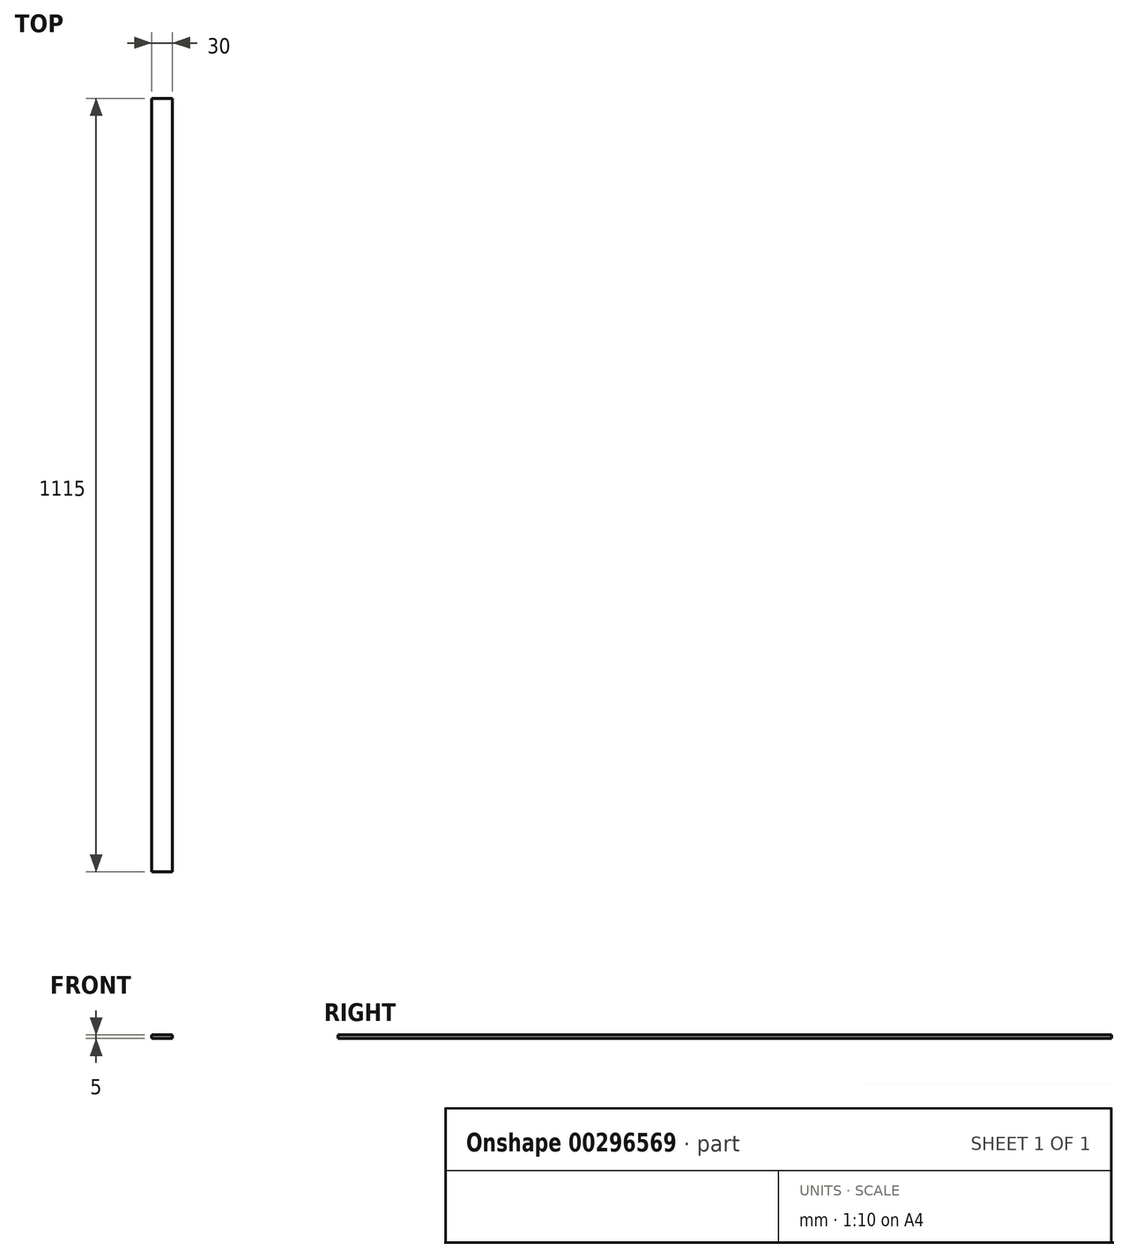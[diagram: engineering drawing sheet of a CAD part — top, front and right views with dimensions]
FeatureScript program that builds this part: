
annotation { "Feature Type Name" : "Feature", "Feature Type Description" : "" }
export const myFeature = defineFeature(function(context is Context, id is Id, definition is map)
    precondition{}
    {
        {
            var Q0;
            Q0=qCreatedBy(makeId("Top.planeOp"),FACE);
            var sketch = newSketch(context, id + "F0", { "sketchPlane" : qUnion([Q0])});
            skLineSegment(sketch, "E0.bottom", {"start": v(15, -557.5) * mm, "end": v(-15, -557.5) * mm});
            skLineSegment(sketch, "E0.top", {"start": v(15, 557.5) * mm, "end": v(-15, 557.5) * mm});
            skLineSegment(sketch, "E0.left", {"start": v(15, -557.5) * mm, "end": v(15, 557.5) * mm});
            skLineSegment(sketch, "E0.right", {"start": v(-15, -557.5) * mm, "end": v(-15, 557.5) * mm});
            skPoint(sketch, "E0.middle", {"position": v(0, 0) * mm});
            skSolve(sketch);
        }
        {
            var Q0;
            Q0=makeQuery(id+"F0.imprint","IMPRINT",FACE,{"disambiguationData":[TD([[makeQuery(id+"F0.imprint","IMPRINT",EDGE,{"derivedFrom":sQuery(id+"F0.wireOp",EDGE,"E0.bottom")}),-1.0]])]});
            extrude(context, id + "F1", {"entities" : qUnion([Q0]), "depth" : 5 * mm});
        }
    });
